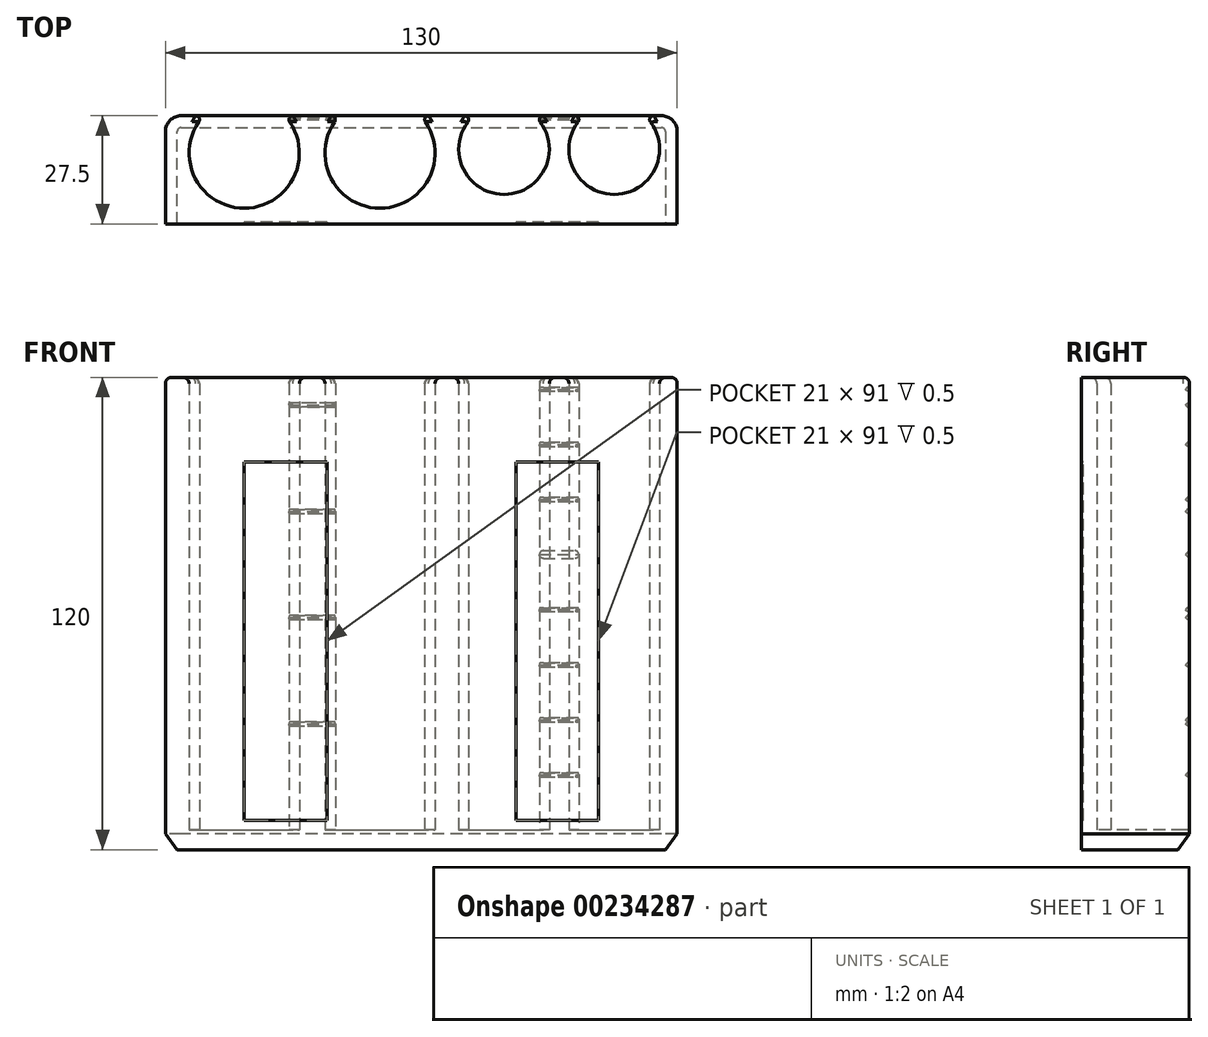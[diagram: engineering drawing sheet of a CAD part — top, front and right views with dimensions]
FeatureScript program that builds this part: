
annotation { "Feature Type Name" : "Feature", "Feature Type Description" : "" }
export const myFeature = defineFeature(function(context is Context, id is Id, definition is map)
    precondition{}
    {
        {
            var Q0;
            Q0=qCreatedBy(makeId("Top.planeOp"),FACE);
            var sketch = newSketch(context, id + "F0", { "sketchPlane" : qUnion([Q0])});
            skLineSegment(sketch, "E0.bottom", {"start": v(-65, 13.75) * mm, "end": v(65, 13.75) * mm});
            skLineSegment(sketch, "E0.top", {"start": v(-65, -13.75) * mm, "end": v(65, -13.75) * mm});
            skLineSegment(sketch, "E0.left", {"start": v(-65, 13.75) * mm, "end": v(-65, -13.75) * mm});
            skLineSegment(sketch, "E0.right", {"start": v(65, 13.75) * mm, "end": v(65, -13.75) * mm});
            skCircle(sketch, "E1", {"center": v(-45, 4.25) * mm, "radius": 14 * mm});
            skCircle(sketch, "E2", {"center": v(49, 5.25) * mm, "radius": 11.5 * mm});
            skCircle(sketch, "E3", {"center": v(-10.5, 4.25) * mm, "radius": 14 * mm});
            skCircle(sketch, "E4", {"center": v(21, 5.25) * mm, "radius": 11.5 * mm});
            skPoint(sketch, "E5", {"position": v(0, 0) * mm});
            skPoint(sketch, "E5.positionSnap0", {"position": v(-65, 0) * mm});
            skPoint(sketch, "E5.positionSnap1", {"position": v(0, 13.75) * mm});
            skSolve(sketch);
        }
        {
            var Q0;
            Q0=makeQuery(id+"F0.imprint","IMPRINT",FACE,{"disambiguationData":[TD([[makeQuery(id+"F0.imprint","IMPRINT",EDGE,{"derivedFrom":sQuery(id+"F0.wireOp",EDGE,"E0.top")}),1.0]])]});
            extrude(context, id + "F1", {"entities" : qUnion([Q0]), "depth" : 115 * mm});
        }
        {
            var Q0;
            Q0=makeQuery(id+"F0.imprint","IMPRINT",FACE,{"disambiguationData":[TD([[makeQuery(id+"F0.imprint","IMPRINT",EDGE,{"derivedFrom":sQuery(id+"F0.wireOp",EDGE,"E0.top")}),1.0]])]});
            var Q1;
            {var subQ0=sQuery(id+"F0.wireOp",EDGE,"E2");var subQ1=sQuery(id+"F0.wireOp",EDGE,"E0.bottom");var subQ2=makeQuery(id+"F0.imprint","INTERSECT",VERTEX,{"disambiguationData":[OD(0.0)],"derivedFrom":[subQ1,subQ0]});Q1=makeQuery(id+"F0.imprint","IMPRINT",FACE,{"disambiguationData":[TD([[makeQuery(id+"F0.imprint","IMPRINT",EDGE,{"disambiguationData":[TD([[subQ2,-1.0]])],"derivedFrom":subQ1}),-1.0]])]});}
            var Q2;
            {var subQ0=sQuery(id+"F0.wireOp",EDGE,"E4");var subQ1=sQuery(id+"F0.wireOp",EDGE,"E0.bottom");var subQ2=makeQuery(id+"F0.imprint","INTERSECT",VERTEX,{"disambiguationData":[OD(0.0)],"derivedFrom":[subQ1,subQ0]});Q2=makeQuery(id+"F0.imprint","IMPRINT",FACE,{"disambiguationData":[TD([[makeQuery(id+"F0.imprint","IMPRINT",EDGE,{"disambiguationData":[TD([[subQ2,-1.0]])],"derivedFrom":subQ1}),-1.0]])]});}
            var Q3;
            {var subQ0=sQuery(id+"F0.wireOp",EDGE,"E3");var subQ1=sQuery(id+"F0.wireOp",EDGE,"E0.bottom");var subQ2=makeQuery(id+"F0.imprint","INTERSECT",VERTEX,{"disambiguationData":[OD(0.0)],"derivedFrom":[subQ1,subQ0]});Q3=makeQuery(id+"F0.imprint","IMPRINT",FACE,{"disambiguationData":[TD([[makeQuery(id+"F0.imprint","IMPRINT",EDGE,{"disambiguationData":[TD([[subQ2,-1.0]])],"derivedFrom":subQ1}),-1.0]])]});}
            var Q4;
            {var subQ0=sQuery(id+"F0.wireOp",EDGE,"E1");var subQ1=sQuery(id+"F0.wireOp",EDGE,"E0.bottom");var subQ2=makeQuery(id+"F0.imprint","INTERSECT",VERTEX,{"disambiguationData":[OD(0.0)],"derivedFrom":[subQ1,subQ0]});Q4=makeQuery(id+"F0.imprint","IMPRINT",FACE,{"disambiguationData":[TD([[makeQuery(id+"F0.imprint","IMPRINT",EDGE,{"disambiguationData":[TD([[subQ2,-1.0]])],"derivedFrom":subQ1}),-1.0]])]});}
            extrude(context, id + "F2", {"entities" : qUnion([Q0, Q1, Q2, Q3, Q4]), "operationType" : NewBodyOperationType.ADD, "oppositeDirection" : true, "depth" : 5 * mm});
        }
        {
            var Q0;
            {var subQ0=sQuery(id+"F0.wireOp",EDGE,"E0.right");var subQ1=sQuery(id+"F0.wireOp",EDGE,"E0.bottom");Q0=makeQuery(id+"F2.boolean.opBoolean","MERGE",EDGE,{"derivedFrom":[makeQuery(id+"F1.opExtrude","SWEPT_EDGE",EDGE,{"disambiguationData":[OSD([subQ1,subQ0])]}),makeQuery(id+"F2.opExtrude","SWEPT_EDGE",EDGE,{"disambiguationData":[OSD([subQ1,subQ0])]})]});}
            var Q1;
            {var subQ0=sQuery(id+"F0.wireOp",EDGE,"E0.left");var subQ1=sQuery(id+"F0.wireOp",EDGE,"E0.bottom");Q1=makeQuery(id+"F2.boolean.opBoolean","MERGE",EDGE,{"derivedFrom":[makeQuery(id+"F1.opExtrude","SWEPT_EDGE",EDGE,{"disambiguationData":[OSD([subQ1,subQ0])]}),makeQuery(id+"F2.opExtrude","SWEPT_EDGE",EDGE,{"disambiguationData":[OSD([subQ1,subQ0])]})]});}
            fillet(context, id + "F3", {"entities" : qUnion([Q0, Q1]), "radius" : 4 * mm, "tangentPropagation" : true, "allowEdgeOverflow" : false});
        }
        {
            var Q0;
            {var subQ0=sQuery(id+"F0.wireOp",EDGE,"E2");var subQ1=sQuery(id+"F0.wireOp",EDGE,"E0.bottom");Q0=makeQuery(id+"F1.opExtrude","SWEPT_EDGE",EDGE,{"disambiguationData":[OSD([subQ1,subQ0]),TDD([makeQuery(id+"F0.imprint","INTERSECT",VERTEX,{"disambiguationData":[OD(1.0)],"derivedFrom":[subQ1,subQ0]})])]});}
            var Q1;
            {var subQ0=sQuery(id+"F0.wireOp",EDGE,"E2");var subQ1=sQuery(id+"F0.wireOp",EDGE,"E0.bottom");Q1=makeQuery(id+"F1.opExtrude","SWEPT_EDGE",EDGE,{"disambiguationData":[OSD([subQ1,subQ0]),TDD([makeQuery(id+"F0.imprint","INTERSECT",VERTEX,{"disambiguationData":[OD(0.0)],"derivedFrom":[subQ1,subQ0]})])]});}
            var Q2;
            {var subQ0=sQuery(id+"F0.wireOp",EDGE,"E4");var subQ1=sQuery(id+"F0.wireOp",EDGE,"E0.bottom");Q2=makeQuery(id+"F1.opExtrude","SWEPT_EDGE",EDGE,{"disambiguationData":[OSD([subQ1,subQ0]),TDD([makeQuery(id+"F0.imprint","INTERSECT",VERTEX,{"disambiguationData":[OD(1.0)],"derivedFrom":[subQ1,subQ0]})])]});}
            var Q3;
            {var subQ0=sQuery(id+"F0.wireOp",EDGE,"E4");var subQ1=sQuery(id+"F0.wireOp",EDGE,"E0.bottom");Q3=makeQuery(id+"F1.opExtrude","SWEPT_EDGE",EDGE,{"disambiguationData":[OSD([subQ1,subQ0]),TDD([makeQuery(id+"F0.imprint","INTERSECT",VERTEX,{"disambiguationData":[OD(0.0)],"derivedFrom":[subQ1,subQ0]})])]});}
            var Q4;
            {var subQ0=sQuery(id+"F0.wireOp",EDGE,"E3");var subQ1=sQuery(id+"F0.wireOp",EDGE,"E0.bottom");Q4=makeQuery(id+"F1.opExtrude","SWEPT_EDGE",EDGE,{"disambiguationData":[OSD([subQ1,subQ0]),TDD([makeQuery(id+"F0.imprint","INTERSECT",VERTEX,{"disambiguationData":[OD(1.0)],"derivedFrom":[subQ1,subQ0]})])]});}
            var Q5;
            {var subQ0=sQuery(id+"F0.wireOp",EDGE,"E3");var subQ1=sQuery(id+"F0.wireOp",EDGE,"E0.bottom");Q5=makeQuery(id+"F1.opExtrude","SWEPT_EDGE",EDGE,{"disambiguationData":[OSD([subQ1,subQ0]),TDD([makeQuery(id+"F0.imprint","INTERSECT",VERTEX,{"disambiguationData":[OD(0.0)],"derivedFrom":[subQ1,subQ0]})])]});}
            var Q6;
            {var subQ0=sQuery(id+"F0.wireOp",EDGE,"E1");var subQ1=sQuery(id+"F0.wireOp",EDGE,"E0.bottom");Q6=makeQuery(id+"F1.opExtrude","SWEPT_EDGE",EDGE,{"disambiguationData":[OSD([subQ1,subQ0]),TDD([makeQuery(id+"F0.imprint","INTERSECT",VERTEX,{"disambiguationData":[OD(0.0)],"derivedFrom":[subQ1,subQ0]})])]});}
            var Q7;
            {var subQ0=sQuery(id+"F0.wireOp",EDGE,"E1");var subQ1=sQuery(id+"F0.wireOp",EDGE,"E0.bottom");Q7=makeQuery(id+"F1.opExtrude","SWEPT_EDGE",EDGE,{"disambiguationData":[OSD([subQ1,subQ0]),TDD([makeQuery(id+"F0.imprint","INTERSECT",VERTEX,{"disambiguationData":[OD(1.0)],"derivedFrom":[subQ1,subQ0]})])]});}
            fillet(context, id + "F4", {"entities" : qUnion([Q0, Q1, Q2, Q3, Q4, Q5, Q6, Q7]), "radius" : 1 * mm, "tangentPropagation" : true, "allowEdgeOverflow" : false});
        }
        {
            var Q0;
            Q0=makeQuery(id+"F1.opExtrude","CAP_EDGE",EDGE,{"disambiguationData":[OSD([sQuery(id+"F0.wireOp",EDGE,"E2")])],"isStart":false});
            fillet(context, id + "F5", {"entities" : qUnion([Q0]), "radius" : 1.5 * mm, "tangentPropagation" : true, "allowEdgeOverflow" : false});
        }
        {
            var Q0;
            Q0=makeQuery(id+"F2.opExtrude","CAP_EDGE",EDGE,{"disambiguationData":[OSD([sQuery(id+"F0.wireOp",EDGE,"E0.bottom")])],"isStart":false});
            chamfer(context, id + "F6", {"entities" : qUnion([Q0]), "chamferType" : ChamferType.TWO_OFFSETS, "width1" : 3 * mm, "oppositeDirection" : false, "width2" : 4 * mm, "tangentPropagation" : true});
        }
        {
            var Q0;
            {var subQ0=sQuery(id+"F0.wireOp",EDGE,"E0.top");Q0=makeQuery(id+"F2.boolean.opBoolean","MERGE",FACE,{"derivedFrom":[makeQuery(id+"F1.opExtrude","SWEPT_FACE",FACE,{"disambiguationData":[OSD([subQ0])]}),makeQuery(id+"F2.opExtrude","SWEPT_FACE",FACE,{"disambiguationData":[OSD([subQ0])]})]});}
            var sketch = newSketch(context, id + "F7", { "sketchPlane" : qUnion([Q0])});
            skLineSegment(sketch, "E6.bottom", {"start": v(45, 2.5) * mm, "end": v(24, 2.5) * mm});
            skLineSegment(sketch, "E6.top", {"start": v(45, 93.5) * mm, "end": v(24, 93.5) * mm});
            skLineSegment(sketch, "E6.left", {"start": v(45, 2.5) * mm, "end": v(45, 93.5) * mm});
            skLineSegment(sketch, "E6.right", {"start": v(24, 2.5) * mm, "end": v(24, 93.5) * mm});
            skLineSegment(sketch, "E7.bottom", {"start": v(-24, 2.5) * mm, "end": v(-45, 2.5) * mm});
            skLineSegment(sketch, "E7.top", {"start": v(-24, 93.5) * mm, "end": v(-45, 93.5) * mm});
            skLineSegment(sketch, "E7.left", {"start": v(-24, 2.5) * mm, "end": v(-24, 93.5) * mm});
            skLineSegment(sketch, "E7.right", {"start": v(-45, 2.5) * mm, "end": v(-45, 93.5) * mm});
            skSolve(sketch);
        }
        {
            var Q0;
            {var subQ0=sQuery(id+"F0.wireOp",EDGE,"E0.bottom");var subQ2=sQuery(id+"F0.wireOp",EDGE,"E4");var subQ3=sQuery(id+"F0.wireOp",EDGE,"E3");var subQ4=sQuery(id+"F0.wireOp",EDGE,"E1");Q0=makeQuery(id+"F2.boolean.opBoolean","MERGE",FACE,{"derivedFrom":[makeQuery(id+"F1.opExtrude","SWEPT_FACE",FACE,{"disambiguationData":[OSD([subQ0]),TDD([makeQuery(id+"F0.imprint","IMPRINT",EDGE,{"disambiguationData":[TD([[makeQuery(id+"F0.imprint","INTERSECT",VERTEX,{"derivedFrom":[subQ0,sQuery(id+"F0.wireOp",EDGE,"E0.left")]}),-1.0]])],"derivedFrom":subQ0})])]}),makeQuery(id+"F1.opExtrude","SWEPT_FACE",FACE,{"disambiguationData":[OSD([subQ0]),TDD([makeQuery(id+"F0.imprint","IMPRINT",EDGE,{"disambiguationData":[TD([[makeQuery(id+"F0.imprint","INTERSECT",VERTEX,{"disambiguationData":[OD(1.0)],"derivedFrom":[subQ0,subQ4]}),-1.0]])],"derivedFrom":subQ0})])]}),makeQuery(id+"F1.opExtrude","SWEPT_FACE",FACE,{"disambiguationData":[OSD([subQ0]),TDD([makeQuery(id+"F0.imprint","IMPRINT",EDGE,{"disambiguationData":[TD([[makeQuery(id+"F0.imprint","INTERSECT",VERTEX,{"disambiguationData":[OD(1.0)],"derivedFrom":[subQ0,subQ3]}),-1.0]])],"derivedFrom":subQ0})])]}),makeQuery(id+"F1.opExtrude","SWEPT_FACE",FACE,{"disambiguationData":[OSD([subQ0]),TDD([makeQuery(id+"F0.imprint","IMPRINT",EDGE,{"disambiguationData":[TD([[makeQuery(id+"F0.imprint","INTERSECT",VERTEX,{"disambiguationData":[OD(1.0)],"derivedFrom":[subQ0,subQ2]}),-1.0]])],"derivedFrom":subQ0})])]}),makeQuery(id+"F1.opExtrude","SWEPT_FACE",FACE,{"disambiguationData":[OSD([subQ0]),TDD([makeQuery(id+"F0.imprint","IMPRINT",EDGE,{"disambiguationData":[TD([[makeQuery(id+"F0.imprint","INTERSECT",VERTEX,{"derivedFrom":[subQ0,sQuery(id+"F0.wireOp",EDGE,"E0.right")]}),1.0]])],"derivedFrom":subQ0})])]}),makeQuery(id+"F2.opExtrude","SWEPT_FACE",FACE,{"disambiguationData":[OSD([subQ0])]})]});}
            var sketch = newSketch(context, id + "F8", { "sketchPlane" : qUnion([Q0])});
            skLineSegment(sketch, "E8.bottom", {"start": v(-39, 13.5) * mm, "end": v(-31, 13.5) * mm});
            skLineSegment(sketch, "E8.top", {"start": v(-39, 14.5) * mm, "end": v(-31, 14.5) * mm});
            skLineSegment(sketch, "E8.left", {"start": v(-39, 13.5) * mm, "end": v(-39, 14.5) * mm});
            skLineSegment(sketch, "E8.right", {"start": v(-31, 13.5) * mm, "end": v(-31, 14.5) * mm});
            skLineSegment(sketch, "E9.bottom", {"start": v(-39, 27.5) * mm, "end": v(-31, 27.5) * mm});
            skLineSegment(sketch, "E9.top", {"start": v(-39, 28.5) * mm, "end": v(-31, 28.5) * mm});
            skLineSegment(sketch, "E9.left", {"start": v(-39, 27.5) * mm, "end": v(-39, 28.5) * mm});
            skLineSegment(sketch, "E9.right", {"start": v(-31, 27.5) * mm, "end": v(-31, 28.5) * mm});
            skLineSegment(sketch, "E10.bottom", {"start": v(-39, 41.5) * mm, "end": v(-31, 41.5) * mm});
            skLineSegment(sketch, "E10.top", {"start": v(-39, 42.5) * mm, "end": v(-31, 42.5) * mm});
            skLineSegment(sketch, "E10.left", {"start": v(-39, 41.5) * mm, "end": v(-39, 42.5) * mm});
            skLineSegment(sketch, "E10.right", {"start": v(-31, 41.5) * mm, "end": v(-31, 42.5) * mm});
            skLineSegment(sketch, "E11.bottom", {"start": v(-39, 55.5) * mm, "end": v(-31, 55.5) * mm});
            skLineSegment(sketch, "E11.top", {"start": v(-39, 56.5) * mm, "end": v(-31, 56.5) * mm});
            skLineSegment(sketch, "E11.left", {"start": v(-39, 55.5) * mm, "end": v(-39, 56.5) * mm});
            skLineSegment(sketch, "E11.right", {"start": v(-31, 55.5) * mm, "end": v(-31, 56.5) * mm});
            skLineSegment(sketch, "E12.bottom", {"start": v(-39, 69) * mm, "end": v(-31, 69) * mm});
            skLineSegment(sketch, "E12.top", {"start": v(-39, 71) * mm, "end": v(-31, 71) * mm});
            skLineSegment(sketch, "E12.left", {"start": v(-39, 69) * mm, "end": v(-39, 71) * mm});
            skLineSegment(sketch, "E12.right", {"start": v(-31, 69) * mm, "end": v(-31, 71) * mm});
            skLineSegment(sketch, "E13.bottom", {"start": v(-39, 83.5) * mm, "end": v(-31, 83.5) * mm});
            skLineSegment(sketch, "E13.top", {"start": v(-39, 84.5) * mm, "end": v(-31, 84.5) * mm});
            skLineSegment(sketch, "E13.left", {"start": v(-39, 83.5) * mm, "end": v(-39, 84.5) * mm});
            skLineSegment(sketch, "E13.right", {"start": v(-31, 83.5) * mm, "end": v(-31, 84.5) * mm});
            skLineSegment(sketch, "E14.bottom", {"start": v(-39, 97.5) * mm, "end": v(-31, 97.5) * mm});
            skLineSegment(sketch, "E14.top", {"start": v(-39, 98.5) * mm, "end": v(-31, 98.5) * mm});
            skLineSegment(sketch, "E14.left", {"start": v(-39, 97.5) * mm, "end": v(-39, 98.5) * mm});
            skLineSegment(sketch, "E14.right", {"start": v(-31, 97.5) * mm, "end": v(-31, 98.5) * mm});
            skLineSegment(sketch, "E15.bottom", {"start": v(22.86, 26.5) * mm, "end": v(32.64, 26.5) * mm});
            skLineSegment(sketch, "E15.top", {"start": v(22.86, 27.5) * mm, "end": v(32.64, 27.5) * mm});
            skLineSegment(sketch, "E15.left", {"start": v(22.86, 26.5) * mm, "end": v(22.86, 27.5) * mm});
            skLineSegment(sketch, "E15.right", {"start": v(32.64, 26.5) * mm, "end": v(32.64, 27.5) * mm});
            skLineSegment(sketch, "E16.bottom", {"start": v(22.86, 53.5) * mm, "end": v(32.64, 53.5) * mm});
            skLineSegment(sketch, "E16.top", {"start": v(22.86, 54.5) * mm, "end": v(32.64, 54.5) * mm});
            skLineSegment(sketch, "E16.left", {"start": v(22.86, 53.5) * mm, "end": v(22.86, 54.5) * mm});
            skLineSegment(sketch, "E16.right", {"start": v(32.64, 53.5) * mm, "end": v(32.64, 54.5) * mm});
            skLineSegment(sketch, "E17.bottom", {"start": v(22.86, 80.5) * mm, "end": v(32.64, 80.5) * mm});
            skLineSegment(sketch, "E17.top", {"start": v(22.86, 81.5) * mm, "end": v(32.64, 81.5) * mm});
            skLineSegment(sketch, "E17.left", {"start": v(22.86, 80.5) * mm, "end": v(22.86, 81.5) * mm});
            skLineSegment(sketch, "E17.right", {"start": v(32.64, 80.5) * mm, "end": v(32.64, 81.5) * mm});
            skLineSegment(sketch, "E18.bottom", {"start": v(-39, 98.5) * mm, "end": v(-44, 98.5) * mm});
            skLineSegment(sketch, "E18.top", {"start": v(-39, 97.5) * mm, "end": v(-44, 97.5) * mm});
            skLineSegment(sketch, "E18.left", {"start": v(-39, 98.5) * mm, "end": v(-39, 97.5) * mm});
            skLineSegment(sketch, "E18.right", {"start": v(-44, 98.5) * mm, "end": v(-44, 97.5) * mm});
            skLineSegment(sketch, "E19.bottom", {"start": v(-31, 98.5) * mm, "end": v(-26, 98.5) * mm});
            skLineSegment(sketch, "E19.top", {"start": v(-31, 97.5) * mm, "end": v(-26, 97.5) * mm});
            skLineSegment(sketch, "E19.left", {"start": v(-31, 98.5) * mm, "end": v(-31, 97.5) * mm});
            skLineSegment(sketch, "E19.right", {"start": v(-26, 98.5) * mm, "end": v(-26, 97.5) * mm});
            skLineSegment(sketch, "E20.bottom", {"start": v(-31, 84.5) * mm, "end": v(-26, 84.5) * mm});
            skLineSegment(sketch, "E20.top", {"start": v(-31, 83.5) * mm, "end": v(-26, 83.5) * mm});
            skLineSegment(sketch, "E20.left", {"start": v(-31, 84.5) * mm, "end": v(-31, 83.5) * mm});
            skLineSegment(sketch, "E20.right", {"start": v(-26, 84.5) * mm, "end": v(-26, 83.5) * mm});
            skLineSegment(sketch, "E21.bottom", {"start": v(-39, 84.5) * mm, "end": v(-44, 84.5) * mm});
            skLineSegment(sketch, "E21.top", {"start": v(-39, 83.5) * mm, "end": v(-44, 83.5) * mm});
            skLineSegment(sketch, "E21.left", {"start": v(-39, 84.5) * mm, "end": v(-39, 83.5) * mm});
            skLineSegment(sketch, "E21.right", {"start": v(-44, 84.5) * mm, "end": v(-44, 83.5) * mm});
            skLineSegment(sketch, "E22.bottom", {"start": v(-31, 71) * mm, "end": v(-26, 71) * mm});
            skLineSegment(sketch, "E22.top", {"start": v(-31, 69) * mm, "end": v(-26, 69) * mm});
            skLineSegment(sketch, "E22.left", {"start": v(-31, 71) * mm, "end": v(-31, 69) * mm});
            skLineSegment(sketch, "E22.right", {"start": v(-26, 71) * mm, "end": v(-26, 69) * mm});
            skLineSegment(sketch, "E23.bottom", {"start": v(-39, 71) * mm, "end": v(-44, 71) * mm});
            skLineSegment(sketch, "E23.top", {"start": v(-39, 69) * mm, "end": v(-44, 69) * mm});
            skLineSegment(sketch, "E23.left", {"start": v(-39, 71) * mm, "end": v(-39, 69) * mm});
            skLineSegment(sketch, "E23.right", {"start": v(-44, 71) * mm, "end": v(-44, 69) * mm});
            skLineSegment(sketch, "E24.bottom", {"start": v(-31, 56.5) * mm, "end": v(-26, 56.5) * mm});
            skLineSegment(sketch, "E24.top", {"start": v(-31, 55.5) * mm, "end": v(-26, 55.5) * mm});
            skLineSegment(sketch, "E24.left", {"start": v(-31, 56.5) * mm, "end": v(-31, 55.5) * mm});
            skLineSegment(sketch, "E24.right", {"start": v(-26, 56.5) * mm, "end": v(-26, 55.5) * mm});
            skLineSegment(sketch, "E25.bottom", {"start": v(-39, 56.5) * mm, "end": v(-44, 56.5) * mm});
            skLineSegment(sketch, "E25.top", {"start": v(-39, 55.5) * mm, "end": v(-44, 55.5) * mm});
            skLineSegment(sketch, "E25.left", {"start": v(-39, 56.5) * mm, "end": v(-39, 55.5) * mm});
            skLineSegment(sketch, "E25.right", {"start": v(-44, 56.5) * mm, "end": v(-44, 55.5) * mm});
            skLineSegment(sketch, "E26.bottom", {"start": v(-39, 42.5) * mm, "end": v(-44, 42.5) * mm});
            skLineSegment(sketch, "E26.top", {"start": v(-39, 41.5) * mm, "end": v(-44, 41.5) * mm});
            skLineSegment(sketch, "E26.left", {"start": v(-39, 42.5) * mm, "end": v(-39, 41.5) * mm});
            skLineSegment(sketch, "E26.right", {"start": v(-44, 42.5) * mm, "end": v(-44, 41.5) * mm});
            skLineSegment(sketch, "E27.bottom", {"start": v(-31, 42.5) * mm, "end": v(-26, 42.5) * mm});
            skLineSegment(sketch, "E27.top", {"start": v(-31, 41.5) * mm, "end": v(-26, 41.5) * mm});
            skLineSegment(sketch, "E27.left", {"start": v(-31, 42.5) * mm, "end": v(-31, 41.5) * mm});
            skLineSegment(sketch, "E27.right", {"start": v(-26, 42.5) * mm, "end": v(-26, 41.5) * mm});
            skLineSegment(sketch, "E28.bottom", {"start": v(-31, 28.5) * mm, "end": v(-26, 28.5) * mm});
            skLineSegment(sketch, "E28.top", {"start": v(-31, 27.5) * mm, "end": v(-26, 27.5) * mm});
            skLineSegment(sketch, "E28.left", {"start": v(-31, 28.5) * mm, "end": v(-31, 27.5) * mm});
            skLineSegment(sketch, "E28.right", {"start": v(-26, 28.5) * mm, "end": v(-26, 27.5) * mm});
            skLineSegment(sketch, "E29.bottom", {"start": v(-39, 28.5) * mm, "end": v(-44, 28.5) * mm});
            skLineSegment(sketch, "E29.top", {"start": v(-39, 27.5) * mm, "end": v(-44, 27.5) * mm});
            skLineSegment(sketch, "E29.left", {"start": v(-39, 28.5) * mm, "end": v(-39, 27.5) * mm});
            skLineSegment(sketch, "E29.right", {"start": v(-44, 28.5) * mm, "end": v(-44, 27.5) * mm});
            skLineSegment(sketch, "E30.bottom", {"start": v(-31, 14.5) * mm, "end": v(-26, 14.5) * mm});
            skLineSegment(sketch, "E30.top", {"start": v(-31, 13.5) * mm, "end": v(-26, 13.5) * mm});
            skLineSegment(sketch, "E30.left", {"start": v(-31, 14.5) * mm, "end": v(-31, 13.5) * mm});
            skLineSegment(sketch, "E30.right", {"start": v(-26, 14.5) * mm, "end": v(-26, 13.5) * mm});
            skLineSegment(sketch, "E31.bottom", {"start": v(-39, 14.5) * mm, "end": v(-44, 14.5) * mm});
            skLineSegment(sketch, "E31.top", {"start": v(-39, 13.5) * mm, "end": v(-44, 13.5) * mm});
            skLineSegment(sketch, "E31.left", {"start": v(-39, 14.5) * mm, "end": v(-39, 13.5) * mm});
            skLineSegment(sketch, "E31.right", {"start": v(-44, 14.5) * mm, "end": v(-44, 13.5) * mm});
            skLineSegment(sketch, "E32.bottom", {"start": v(32.64, 27.5) * mm, "end": v(37.64, 27.5) * mm});
            skLineSegment(sketch, "E32.top", {"start": v(32.64, 26.5) * mm, "end": v(37.64, 26.5) * mm});
            skLineSegment(sketch, "E32.left", {"start": v(32.64, 27.5) * mm, "end": v(32.64, 26.5) * mm});
            skLineSegment(sketch, "E32.right", {"start": v(37.64, 27.5) * mm, "end": v(37.64, 26.5) * mm});
            skLineSegment(sketch, "E33.bottom", {"start": v(22.86, 27.5) * mm, "end": v(17.86, 27.5) * mm});
            skLineSegment(sketch, "E33.top", {"start": v(22.86, 26.5) * mm, "end": v(17.86, 26.5) * mm});
            skLineSegment(sketch, "E33.left", {"start": v(22.86, 27.5) * mm, "end": v(22.86, 26.5) * mm});
            skLineSegment(sketch, "E33.right", {"start": v(17.86, 27.5) * mm, "end": v(17.86, 26.5) * mm});
            skLineSegment(sketch, "E34.bottom", {"start": v(32.64, 54.5) * mm, "end": v(37.64, 54.5) * mm});
            skLineSegment(sketch, "E34.top", {"start": v(32.64, 53.5) * mm, "end": v(37.64, 53.5) * mm});
            skLineSegment(sketch, "E34.left", {"start": v(32.64, 54.5) * mm, "end": v(32.64, 53.5) * mm});
            skLineSegment(sketch, "E34.right", {"start": v(37.64, 54.5) * mm, "end": v(37.64, 53.5) * mm});
            skLineSegment(sketch, "E35.bottom", {"start": v(22.86, 54.5) * mm, "end": v(17.86, 54.5) * mm});
            skLineSegment(sketch, "E35.top", {"start": v(22.86, 53.5) * mm, "end": v(17.86, 53.5) * mm});
            skLineSegment(sketch, "E35.left", {"start": v(22.86, 54.5) * mm, "end": v(22.86, 53.5) * mm});
            skLineSegment(sketch, "E35.right", {"start": v(17.86, 54.5) * mm, "end": v(17.86, 53.5) * mm});
            skLineSegment(sketch, "E36.bottom", {"start": v(32.64, 81.5) * mm, "end": v(37.64, 81.5) * mm});
            skLineSegment(sketch, "E36.top", {"start": v(32.64, 80.5) * mm, "end": v(37.64, 80.5) * mm});
            skLineSegment(sketch, "E36.left", {"start": v(32.64, 81.5) * mm, "end": v(32.64, 80.5) * mm});
            skLineSegment(sketch, "E36.right", {"start": v(37.64, 81.5) * mm, "end": v(37.64, 80.5) * mm});
            skLineSegment(sketch, "E37.bottom", {"start": v(22.86, 81.5) * mm, "end": v(17.86, 81.5) * mm});
            skLineSegment(sketch, "E37.top", {"start": v(22.86, 80.5) * mm, "end": v(17.86, 80.5) * mm});
            skLineSegment(sketch, "E37.left", {"start": v(22.86, 81.5) * mm, "end": v(22.86, 80.5) * mm});
            skLineSegment(sketch, "E37.right", {"start": v(17.86, 81.5) * mm, "end": v(17.86, 80.5) * mm});
            skLineSegment(sketch, "E38.bottom", {"start": v(20.14, 108.5) * mm, "end": v(35.14, 108.5) * mm});
            skLineSegment(sketch, "E38.top", {"start": v(20.14, 107.5) * mm, "end": v(35.14, 107.5) * mm});
            skLineSegment(sketch, "E38.left", {"start": v(20.14, 108.5) * mm, "end": v(20.14, 107.5) * mm});
            skLineSegment(sketch, "E38.right", {"start": v(35.14, 108.5) * mm, "end": v(35.14, 107.5) * mm});
            skLineSegment(sketch, "E39.bottom", {"start": v(-39, 112.5) * mm, "end": v(-31, 112.5) * mm});
            skLineSegment(sketch, "E39.top", {"start": v(-39, 111.5) * mm, "end": v(-31, 111.5) * mm});
            skLineSegment(sketch, "E39.left", {"start": v(-39, 112.5) * mm, "end": v(-39, 111.5) * mm});
            skLineSegment(sketch, "E39.right", {"start": v(-31, 112.5) * mm, "end": v(-31, 111.5) * mm});
            skLineSegment(sketch, "E40.bottom", {"start": v(-31, 112.5) * mm, "end": v(-26, 112.5) * mm});
            skLineSegment(sketch, "E40.top", {"start": v(-31, 111.5) * mm, "end": v(-26, 111.5) * mm});
            skLineSegment(sketch, "E40.right", {"start": v(-26, 112.5) * mm, "end": v(-26, 111.5) * mm});
            skLineSegment(sketch, "E41.bottom", {"start": v(-39, 112.5) * mm, "end": v(-44, 112.5) * mm});
            skLineSegment(sketch, "E41.top", {"start": v(-39, 111.5) * mm, "end": v(-44, 111.5) * mm});
            skLineSegment(sketch, "E41.right", {"start": v(-44, 112.5) * mm, "end": v(-44, 111.5) * mm});
            skSolve(sketch);
        }
        {
            var Q0;
            Q0 = qSketchRegion(id + "F8", true);
            extrude(context, id + "F9", {"entities" : qUnion([Q0]), "operationType" : NewBodyOperationType.REMOVE, "oppositeDirection" : true, "depth" : 1 * mm});
        }
        {
            var Q0;
            Q0=makeQuery(id+"F9.boolean.opBoolean","COPY",EDGE,{"derivedFrom":makeQuery(id+"F9.opExtrude","CAP_EDGE",EDGE,{"disambiguationData":[OSD([sQuery(id+"F8.wireOp",EDGE,"E14.bottom"),sQuery(id+"F8.wireOp",EDGE,"E18.top"),sQuery(id+"F8.wireOp",EDGE,"E19.top")])],"isStart":false})});
            var Q1;
            Q1=makeQuery(id+"F9.boolean.opBoolean","COPY",EDGE,{"derivedFrom":makeQuery(id+"F9.opExtrude","CAP_EDGE",EDGE,{"disambiguationData":[OSD([sQuery(id+"F8.wireOp",EDGE,"E14.top"),sQuery(id+"F8.wireOp",EDGE,"E18.bottom"),sQuery(id+"F8.wireOp",EDGE,"E19.bottom")])],"isStart":false})});
            var Q2;
            Q2=makeQuery(id+"F9.boolean.opBoolean","COPY",EDGE,{"derivedFrom":makeQuery(id+"F9.opExtrude","CAP_EDGE",EDGE,{"disambiguationData":[OSD([sQuery(id+"F8.wireOp",EDGE,"E13.top"),sQuery(id+"F8.wireOp",EDGE,"E20.bottom"),sQuery(id+"F8.wireOp",EDGE,"E21.bottom")])],"isStart":false})});
            var Q3;
            Q3=makeQuery(id+"F9.boolean.opBoolean","COPY",EDGE,{"derivedFrom":makeQuery(id+"F9.opExtrude","CAP_EDGE",EDGE,{"disambiguationData":[OSD([sQuery(id+"F8.wireOp",EDGE,"E13.bottom"),sQuery(id+"F8.wireOp",EDGE,"E20.top"),sQuery(id+"F8.wireOp",EDGE,"E21.top")])],"isStart":false})});
            var Q4;
            Q4=makeQuery(id+"F9.boolean.opBoolean","COPY",EDGE,{"derivedFrom":makeQuery(id+"F9.opExtrude","CAP_EDGE",EDGE,{"disambiguationData":[OSD([sQuery(id+"F8.wireOp",EDGE,"E11.bottom"),sQuery(id+"F8.wireOp",EDGE,"E24.top"),sQuery(id+"F8.wireOp",EDGE,"E25.top")])],"isStart":false})});
            var Q5;
            Q5=makeQuery(id+"F9.boolean.opBoolean","COPY",EDGE,{"derivedFrom":makeQuery(id+"F9.opExtrude","CAP_EDGE",EDGE,{"disambiguationData":[OSD([sQuery(id+"F8.wireOp",EDGE,"E10.bottom"),sQuery(id+"F8.wireOp",EDGE,"E26.top"),sQuery(id+"F8.wireOp",EDGE,"E27.top")])],"isStart":false})});
            var Q6;
            Q6=makeQuery(id+"F9.boolean.opBoolean","COPY",EDGE,{"derivedFrom":makeQuery(id+"F9.opExtrude","CAP_EDGE",EDGE,{"disambiguationData":[OSD([sQuery(id+"F8.wireOp",EDGE,"E9.bottom"),sQuery(id+"F8.wireOp",EDGE,"E28.top"),sQuery(id+"F8.wireOp",EDGE,"E29.top")])],"isStart":false})});
            var Q7;
            Q7=makeQuery(id+"F9.boolean.opBoolean","COPY",EDGE,{"derivedFrom":makeQuery(id+"F9.opExtrude","CAP_EDGE",EDGE,{"disambiguationData":[OSD([sQuery(id+"F8.wireOp",EDGE,"E8.bottom"),sQuery(id+"F8.wireOp",EDGE,"E30.top"),sQuery(id+"F8.wireOp",EDGE,"E31.top")])],"isStart":false})});
            var Q8;
            Q8=makeQuery(id+"F9.boolean.opBoolean","COPY",EDGE,{"derivedFrom":makeQuery(id+"F9.opExtrude","CAP_EDGE",EDGE,{"disambiguationData":[OSD([sQuery(id+"F8.wireOp",EDGE,"E15.bottom"),sQuery(id+"F8.wireOp",EDGE,"E32.top"),sQuery(id+"F8.wireOp",EDGE,"E33.top")])],"isStart":false})});
            var Q9;
            Q9=makeQuery(id+"F9.boolean.opBoolean","COPY",EDGE,{"derivedFrom":makeQuery(id+"F9.opExtrude","CAP_EDGE",EDGE,{"disambiguationData":[OSD([sQuery(id+"F8.wireOp",EDGE,"E16.bottom"),sQuery(id+"F8.wireOp",EDGE,"E34.top"),sQuery(id+"F8.wireOp",EDGE,"E35.top")])],"isStart":false})});
            var Q10;
            Q10=makeQuery(id+"F9.boolean.opBoolean","COPY",EDGE,{"derivedFrom":makeQuery(id+"F9.opExtrude","CAP_EDGE",EDGE,{"disambiguationData":[OSD([sQuery(id+"F8.wireOp",EDGE,"E17.bottom"),sQuery(id+"F8.wireOp",EDGE,"E36.top"),sQuery(id+"F8.wireOp",EDGE,"E37.top")])],"isStart":false})});
            var Q11;
            Q11=makeQuery(id+"F9.boolean.opBoolean","COPY",EDGE,{"derivedFrom":makeQuery(id+"F9.opExtrude","CAP_EDGE",EDGE,{"disambiguationData":[OSD([sQuery(id+"F8.wireOp",EDGE,"E11.top"),sQuery(id+"F8.wireOp",EDGE,"E24.bottom"),sQuery(id+"F8.wireOp",EDGE,"E25.bottom")])],"isStart":false})});
            var Q12;
            Q12=makeQuery(id+"F9.boolean.opBoolean","COPY",EDGE,{"derivedFrom":makeQuery(id+"F9.opExtrude","CAP_EDGE",EDGE,{"disambiguationData":[OSD([sQuery(id+"F8.wireOp",EDGE,"E10.top"),sQuery(id+"F8.wireOp",EDGE,"E26.bottom"),sQuery(id+"F8.wireOp",EDGE,"E27.bottom")])],"isStart":false})});
            var Q13;
            Q13=makeQuery(id+"F9.boolean.opBoolean","COPY",EDGE,{"derivedFrom":makeQuery(id+"F9.opExtrude","CAP_EDGE",EDGE,{"disambiguationData":[OSD([sQuery(id+"F8.wireOp",EDGE,"E9.top"),sQuery(id+"F8.wireOp",EDGE,"E28.bottom"),sQuery(id+"F8.wireOp",EDGE,"E29.bottom")])],"isStart":false})});
            var Q14;
            Q14=makeQuery(id+"F9.boolean.opBoolean","COPY",EDGE,{"derivedFrom":makeQuery(id+"F9.opExtrude","CAP_EDGE",EDGE,{"disambiguationData":[OSD([sQuery(id+"F8.wireOp",EDGE,"E8.top"),sQuery(id+"F8.wireOp",EDGE,"E30.bottom"),sQuery(id+"F8.wireOp",EDGE,"E31.bottom")])],"isStart":false})});
            var Q15;
            Q15=makeQuery(id+"F9.boolean.opBoolean","COPY",EDGE,{"derivedFrom":makeQuery(id+"F9.opExtrude","CAP_EDGE",EDGE,{"disambiguationData":[OSD([sQuery(id+"F8.wireOp",EDGE,"E15.top"),sQuery(id+"F8.wireOp",EDGE,"E32.bottom"),sQuery(id+"F8.wireOp",EDGE,"E33.bottom")])],"isStart":false})});
            var Q16;
            Q16=makeQuery(id+"F9.boolean.opBoolean","COPY",EDGE,{"derivedFrom":makeQuery(id+"F9.opExtrude","CAP_EDGE",EDGE,{"disambiguationData":[OSD([sQuery(id+"F8.wireOp",EDGE,"E16.top"),sQuery(id+"F8.wireOp",EDGE,"E34.bottom"),sQuery(id+"F8.wireOp",EDGE,"E35.bottom")])],"isStart":false})});
            var Q17;
            Q17=makeQuery(id+"F9.boolean.opBoolean","COPY",EDGE,{"derivedFrom":makeQuery(id+"F9.opExtrude","CAP_EDGE",EDGE,{"disambiguationData":[OSD([sQuery(id+"F8.wireOp",EDGE,"E17.top"),sQuery(id+"F8.wireOp",EDGE,"E36.bottom"),sQuery(id+"F8.wireOp",EDGE,"E37.bottom")])],"isStart":false})});
            var Q18;
            Q18=makeQuery(id+"F9.boolean.opBoolean","COPY",EDGE,{"derivedFrom":makeQuery(id+"F9.opExtrude","CAP_EDGE",EDGE,{"disambiguationData":[OSD([sQuery(id+"F8.wireOp",EDGE,"E38.bottom")])],"isStart":false})});
            var Q19;
            Q19=makeQuery(id+"F9.boolean.opBoolean","COPY",EDGE,{"derivedFrom":makeQuery(id+"F9.opExtrude","CAP_EDGE",EDGE,{"disambiguationData":[OSD([sQuery(id+"F8.wireOp",EDGE,"E38.top")])],"isStart":false})});
            var Q20;
            Q20=makeQuery(id+"F9.boolean.opBoolean","COPY",EDGE,{"derivedFrom":makeQuery(id+"F9.opExtrude","CAP_EDGE",EDGE,{"disambiguationData":[OSD([sQuery(id+"F8.wireOp",EDGE,"E39.top"),sQuery(id+"F8.wireOp",EDGE,"E40.top"),sQuery(id+"F8.wireOp",EDGE,"E41.top")])],"isStart":false})});
            var Q21;
            Q21=makeQuery(id+"F9.boolean.opBoolean","COPY",EDGE,{"derivedFrom":makeQuery(id+"F9.opExtrude","CAP_EDGE",EDGE,{"disambiguationData":[OSD([sQuery(id+"F8.wireOp",EDGE,"E39.bottom"),sQuery(id+"F8.wireOp",EDGE,"E40.bottom"),sQuery(id+"F8.wireOp",EDGE,"E41.bottom")])],"isStart":false})});
            chamfer(context, id + "F10", {"entities" : qUnion([Q0, Q1, Q2, Q3, Q4, Q5, Q6, Q7, Q8, Q9, Q10, Q11, Q12, Q13, Q14, Q15, Q16, Q17, Q18, Q19, Q20, Q21]), "width" : 0.5 * mm, "tangentPropagation" : true});
        }
        {
            var Q0;
            Q0=makeQuery(id+"F9.boolean.opBoolean","COPY",EDGE,{"derivedFrom":makeQuery(id+"F9.opExtrude","CAP_EDGE",EDGE,{"disambiguationData":[OSD([sQuery(id+"F8.wireOp",EDGE,"E12.top"),sQuery(id+"F8.wireOp",EDGE,"E22.bottom"),sQuery(id+"F8.wireOp",EDGE,"E23.bottom")])],"isStart":false})});
            var Q1;
            Q1=makeQuery(id+"F9.boolean.opBoolean","COPY",EDGE,{"derivedFrom":makeQuery(id+"F9.opExtrude","CAP_EDGE",EDGE,{"disambiguationData":[OSD([sQuery(id+"F8.wireOp",EDGE,"E12.bottom"),sQuery(id+"F8.wireOp",EDGE,"E22.top"),sQuery(id+"F8.wireOp",EDGE,"E23.top")])],"isStart":false})});
            chamfer(context, id + "F11", {"entities" : qUnion([Q0, Q1]), "width" : 1 * mm, "tangentPropagation" : true});
        }
        {
            var Q0;
            Q0 = qSketchRegion(id + "F7", true);
            extrude(context, id + "F12", {"entities" : qUnion([Q0]), "operationType" : NewBodyOperationType.REMOVE, "oppositeDirection" : true, "depth" : 0.5 * mm});
        }
    });
